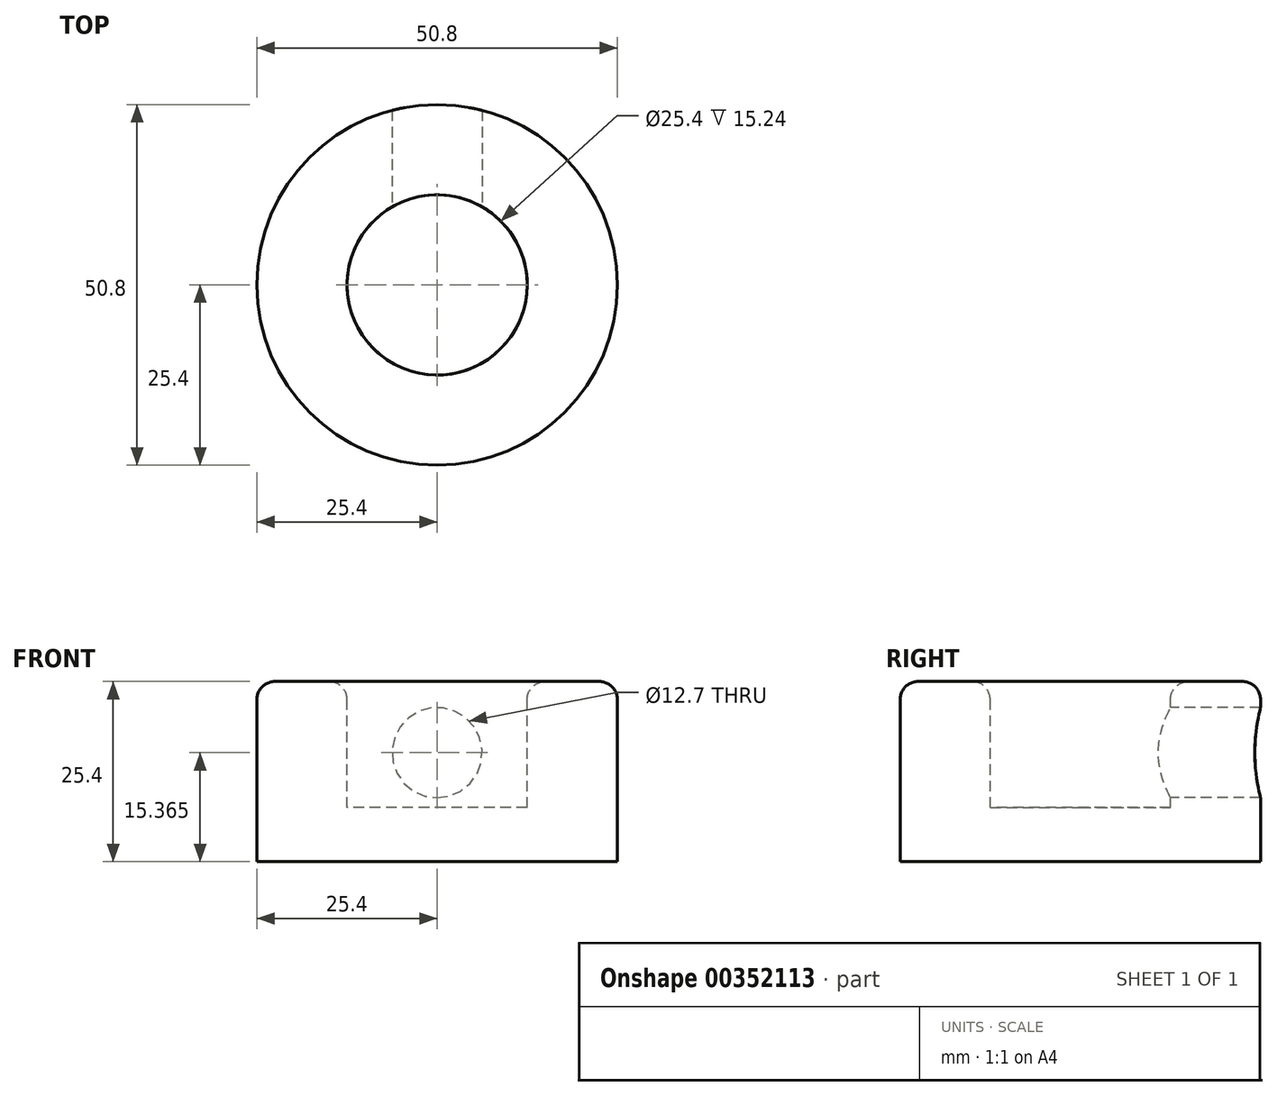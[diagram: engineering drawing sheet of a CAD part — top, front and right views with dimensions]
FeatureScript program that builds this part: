
annotation { "Feature Type Name" : "Feature", "Feature Type Description" : "" }
export const myFeature = defineFeature(function(context is Context, id is Id, definition is map)
    precondition{}
    {
        {
            var Q0;
            Q0=qCreatedBy(makeId("Front.planeOp"),FACE);
            var sketch = newSketch(context, id + "F0", { "sketchPlane" : qUnion([Q0]), "disableImprinting" : false});
            skLineSegment(sketch, "E0", {"start": v(0, 0) * mm, "end": v(25.4, 0) * mm});
            skLineSegment(sketch, "E1", {"start": v(25.4, 0) * mm, "end": v(25.4, 25.4) * mm});
            skLineSegment(sketch, "E2", {"start": v(25.4, 25.4) * mm, "end": v(12.7, 25.4) * mm});
            skLineSegment(sketch, "E3", {"start": v(12.7, 25.4) * mm, "end": v(12.7, 7.62) * mm});
            skLineSegment(sketch, "E4", {"start": v(12.7, 7.62) * mm, "end": v(0, 7.62) * mm});
            skLineSegment(sketch, "E5", {"start": v(0, 7.62) * mm, "end": v(0, 0) * mm});
            skSolve(sketch);
        }
        {
            var Q0;
            Q0=makeQuery(id+"F0.imprint","IMPRINT",FACE,{"disambiguationData":[TD([[makeQuery(id+"F0.imprint","IMPRINT",EDGE,{"derivedFrom":sQuery(id+"F0.wireOp",EDGE,"E0")}),1.0]])]});
            var Q1;
            Q1=sQuery(id+"F0.wireOp",EDGE,"E5");
            revolve(context, id + "F1", {"entities" : qUnion([Q0]), "axis" : qUnion([Q1]), "revolveType" : RevolveType.FULL});
        }
        {
            var Q0;
            Q0=makeQuery(id+"F1.opRevolve","SWEPT_EDGE",EDGE,{"disambiguationData":[OSD([sQuery(id+"F0.wireOp",EDGE,"E1"),sQuery(id+"F0.wireOp",EDGE,"E2")])]});
            var Q1;
            Q1=makeQuery(id+"F1.opRevolve","SWEPT_EDGE",EDGE,{"disambiguationData":[OSD([sQuery(id+"F0.wireOp",EDGE,"E2"),sQuery(id+"F0.wireOp",EDGE,"E3")])]});
            fillet(context, id + "F2", {"entities" : qUnion([Q0, Q1]), "radius" : 2.54 * mm, "tangentPropagation" : true, "allowEdgeOverflow" : false});
        }
        {
            var Q0;
            Q0=qCreatedBy(makeId("Front.planeOp"),FACE);
            var sketch = newSketch(context, id + "F3", { "sketchPlane" : qUnion([Q0])});
            skCircle(sketch, "E6", {"center": v(0, 15.37) * mm, "radius": 6.35 * mm});
            skSolve(sketch);
        }
        {
            var Q0;
            Q0 = qSketchRegion(id + "F3", true);
            extrude(context, id + "F4", {"entities" : qUnion([Q0]), "operationType" : NewBodyOperationType.REMOVE, "endBound" : BoundingType.THROUGH_ALL, "oppositeDirection" : true, "depth" : 25.4 * mm});
        }
    });
